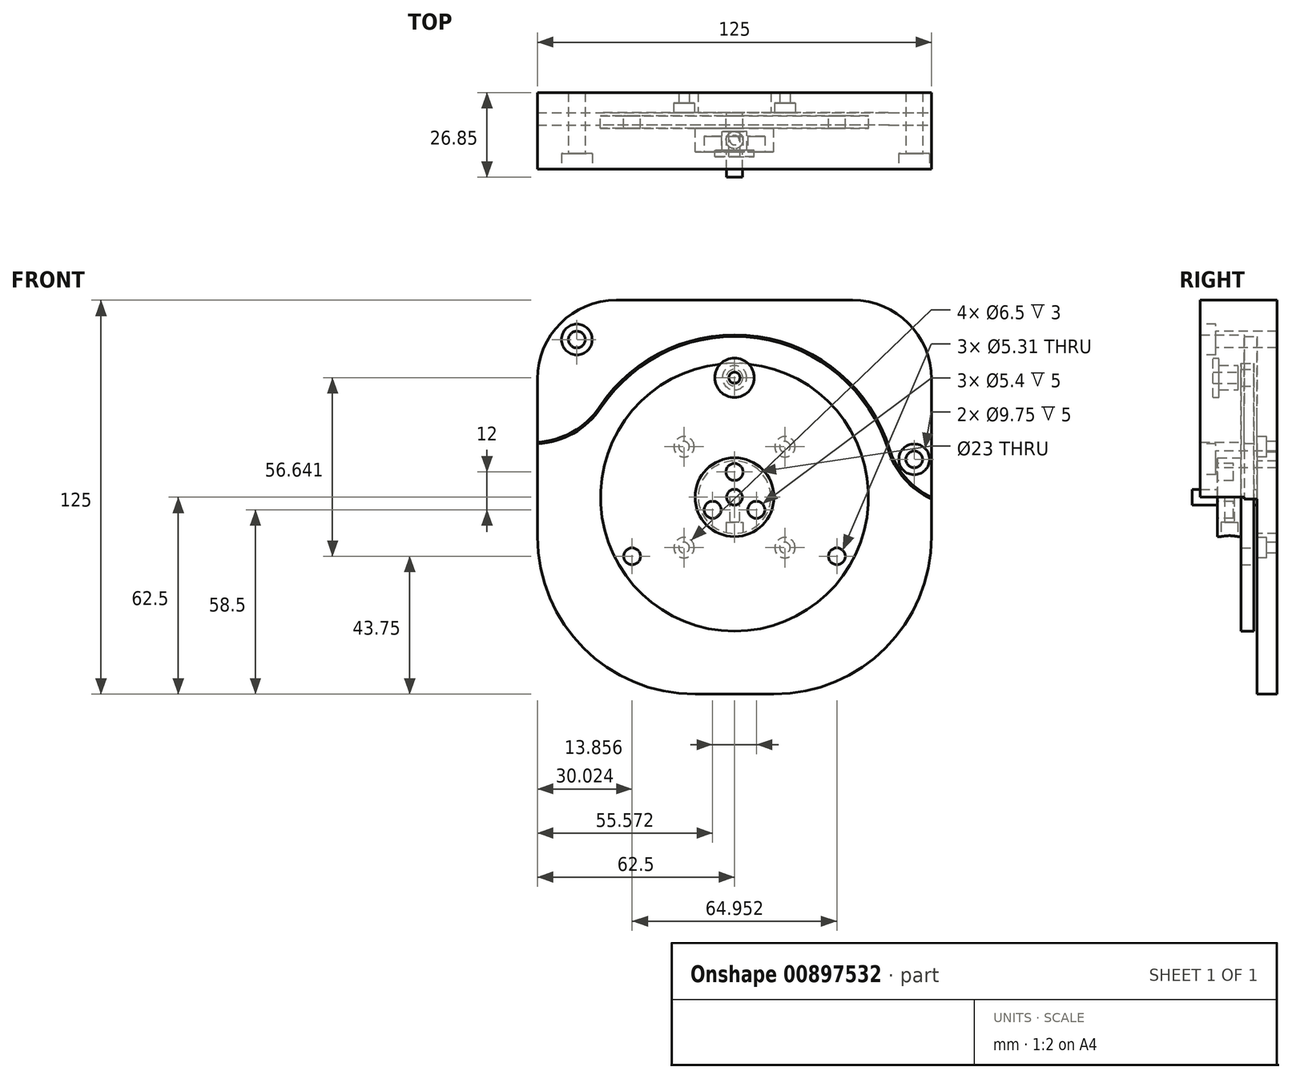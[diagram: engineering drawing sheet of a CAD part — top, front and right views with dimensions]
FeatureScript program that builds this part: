
annotation { "Feature Type Name" : "Feature", "Feature Type Description" : "" }
export const myFeature = defineFeature(function(context is Context, id is Id, definition is map)
    precondition{}
    {
        {
            var Q0;
            Q0=qCreatedBy(makeId("Front.planeOp"),FACE);
            var sketch = newSketch(context, id + "F0", { "sketchPlane" : qUnion([Q0])});
            skLineSegment(sketch, "E0.bottom", {"start": v(62.5, 62.5) * mm, "end": v(-62.5, 62.5) * mm});
            skLineSegment(sketch, "E0.top", {"start": v(62.5, -62.5) * mm, "end": v(-62.5, -62.5) * mm});
            skLineSegment(sketch, "E0.left", {"start": v(62.5, 62.5) * mm, "end": v(62.5, -62.5) * mm});
            skLineSegment(sketch, "E0.right", {"start": v(-62.5, 62.5) * mm, "end": v(-62.5, -62.5) * mm});
            skPoint(sketch, "E0.middle", {"position": v(0, 0) * mm});
            skSolve(sketch);
        }
        {
            var Q0;
            Q0=qCreatedBy(makeId("Front.planeOp"),FACE);
            var sketch = newSketch(context, id + "F1", { "sketchPlane" : qUnion([Q0])});
            skCircle(sketch, "E1", {"center": v(0, 0) * mm, "radius": 11.5 * mm});
            skSolve(sketch);
        }
        {
            var Q0;
            Q0=qCreatedBy(makeId("Front.planeOp"),FACE);
            var sketch = newSketch(context, id + "F2", { "sketchPlane" : qUnion([Q0])});
            skLineSegment(sketch, "E2.bottom", {"start": v(16, 16) * mm, "end": v(-16, 16) * mm, "construction": true});
            skLineSegment(sketch, "E2.top", {"start": v(16, -16) * mm, "end": v(-16, -16) * mm, "construction": true});
            skLineSegment(sketch, "E2.left", {"start": v(16, 16) * mm, "end": v(16, -16) * mm, "construction": true});
            skLineSegment(sketch, "E2.right", {"start": v(-16, 16) * mm, "end": v(-16, -16) * mm, "construction": true});
            skPoint(sketch, "E2.middle", {"position": v(0, 0) * mm});
            skSolve(sketch);
        }
        {
            var Q0;
            Q0 = qSketchRegion(id + "F0", true);
            extrude(context, id + "F3", {"entities" : qUnion([Q0]), "oppositeDirection" : true, "depth" : 6.35 * mm, "offsetDistance" : 25 * mm});
        }
        {
            var Q0;
            Q0=sQuery(id+"F2.wireOp",VERTEX,"E2.bottom.end");
            var Q1;
            Q1=sQuery(id+"F2.wireOp",VERTEX,"E2.bottom.start");
            var Q2;
            Q2=sQuery(id+"F2.wireOp",VERTEX,"E2.top.end");
            var Q3;
            Q3=sQuery(id+"F2.wireOp",VERTEX,"E2.top.start");
            var Q4;
            Q4=makeQuery(id+"F3.opExtrude","SWEPT_BODY",BODY,{"disambiguationData":[OSD([sQuery(id+"F0.wireOp",EDGE,"E0.bottom"),sQuery(id+"F0.wireOp",EDGE,"E0.top"),sQuery(id+"F0.wireOp",EDGE,"E0.left"),sQuery(id+"F0.wireOp",EDGE,"E0.right")])]});
            hole(context, id + "F4", {"style" : HoleStyle.C_BORE, "endStyle" : HoleEndStyle.THROUGH, "standardTappedOrClearance" : lookupTablePath({ "fit" : "Normal", "standard" : "ISO", "size" : "M3", "type" : "Clearance" }), "standardBlindInLast" : lookupTablePath({ "fit" : "Normal", "standard" : "ISO", "engagement" : "75%", "pitch" : "0.5 mm", "size" : "M3", "type" : "Clearance & tapped" }), "holeDiameter" : 3.4 * mm, "cBoreDiameter" : 6.5 * mm, "cBoreDepth" : 3 * mm, "majorDiameter" : 5 * mm, "isTappedThrough" : true, "tappedDepth" : 4.5 * mm, "tapClearance" : 3, "startFromSketch" : true, "locations" : qUnion([Q0, Q1, Q2, Q3]), "scope" : qUnion([Q4])});
        }
        {
            var Q0;
            Q0=makeQuery(id+"F1.imprint","IMPRINT",FACE,{"disambiguationData":[TD([[makeQuery(id+"F1.imprint","IMPRINT",EDGE,{"derivedFrom":sQuery(id+"F1.wireOp",EDGE,"E1")}),1.0]])]});
            extrude(context, id + "F5", {"entities" : qUnion([Q0]), "operationType" : NewBodyOperationType.REMOVE, "endBound" : BoundingType.THROUGH_ALL, "oppositeDirection" : true, "depth" : 25 * mm, "offsetDistance" : 25 * mm});
        }
        {
            var Q0;
            Q0=qCreatedBy(makeId("Front.planeOp"),FACE);
            var sketch = newSketch(context, id + "F6", { "sketchPlane" : qUnion([Q0])});
            skCircle(sketch, "E3", {"center": v(0, 0) * mm, "radius": 2.5 * mm});
            skSolve(sketch);
        }
        {
            var Q0;
            Q0 = qSketchRegion(id + "F6", true);
            extrude(context, id + "F7", {"entities" : qUnion([Q0]), "depth" : (22 - 1.5) * mm, "offsetDistance" : 25 * mm});
        }
        {
            var Q0;
            Q0=qCreatedBy(makeId("Front.planeOp"),FACE);
            var sketch = newSketch(context, id + "F8", { "sketchPlane" : qUnion([Q0])});
            skCircle(sketch, "E4", {"center": v(0, 0) * mm, "radius": 37.5 * mm, "construction": true});
            skCircle(sketch, "E5", {"center": v(0, 37.5) * mm, "radius": 11 * mm, "construction": true});
            skArc(sketch, "E6", {"start": v(51.5, 0) * mm, "mid": v(8.88, 50.73) * mm, "end": v(-48.44, 17.5) * mm});
            skLineSegment(sketch, "E7", {"start": v(0, 51.5) * mm, "end": v(0, 48.5) * mm, "construction": true});
            skCircle(sketch, "E8", {"center": v(0, 0) * mm, "radius": 42.5 * mm});
            skLineSegment(sketch, "E9", {"start": v(-48.44, 17.5) * mm, "end": v(-62.5, 17.5) * mm});
            skLineSegment(sketch, "E10", {"start": v(-62.5, 17.5) * mm, "end": v(-62.5, 62.5) * mm});
            skLineSegment(sketch, "E11", {"start": v(-62.5, 62.5) * mm, "end": v(62.5, 62.5) * mm});
            skLineSegment(sketch, "E12", {"start": v(62.5, 62.5) * mm, "end": v(62.5, 0) * mm});
            skLineSegment(sketch, "E13", {"start": v(62.5, 0) * mm, "end": v(51.5, 0) * mm});
            skCircle(sketch, "E14", {"center": v(0, 37.5) * mm, "radius": 2.65 * mm, "construction": true});
            skLineSegment(sketch, "E15", {"start": v(0, 37.5) * mm, "end": v(0, 0) * mm, "construction": true});
            skLineSegment(sketch, "E16", {"start": v(0, 0) * mm, "end": v(-32.48, -18.75) * mm, "construction": true});
            skLineSegment(sketch, "E17", {"start": v(0, 0) * mm, "end": v(32.48, -18.75) * mm, "construction": true});
            skPoint(sketch, "E18", {"position": v(0, 50) * mm});
            skSolve(sketch);
        }
        {
            var Q0;
            Q0=makeQuery(id+"F8.imprint","IMPRINT",FACE,{"disambiguationData":[TD([[makeQuery(id+"F8.imprint","IMPRINT",EDGE,{"derivedFrom":sQuery(id+"F8.wireOp",EDGE,"E6")}),-1.0]])]});
            extrude(context, id + "F9", {"entities" : qUnion([Q0]), "depth" : 18 * mm, "offsetDistance" : 25 * mm});
        }
        {
            var Q0;
            Q0=qCreatedBy(makeId("Front.planeOp"),FACE);
            cPlane(context, id + "F10", {"entities" : qUnion([Q0]), "cplaneType" : CPlaneType.OFFSET, "offset" : 1 * mm, "width" : 150 * mm, "height" : 150 * mm});
        }
        {
            var Q0;
            Q0=qCreatedBy(id+"F10.planeOp",FACE);
            var sketch = newSketch(context, id + "F11", { "sketchPlane" : qUnion([Q0])});
            skCircle(sketch, "E19.0", {"center": v(0, 0) * mm, "radius": 42.5 * mm});
            skCircle(sketch, "E20", {"center": v(0, 0) * mm, "radius": 2.5 * mm});
            skCircle(sketch, "E21", {"center": v(0, 37.9) * mm, "radius": 2.65 * mm});
            skCircle(sketch, "E22", {"center": v(-32.48, -18.75) * mm, "radius": 2.65 * mm});
            skCircle(sketch, "E23", {"center": v(32.48, -18.75) * mm, "radius": 2.65 * mm});
            skSolve(sketch);
        }
        {
            var Q0;
            Q0 = qSketchRegion(id + "F11", true);
            extrude(context, id + "F12", {"entities" : qUnion([Q0]), "depth" : 4 * mm, "offsetDistance" : 25 * mm});
        }
        {
            var Q0;
            Q0=makeQuery(id+"F12.opExtrude","CAP_FACE",FACE,{"disambiguationData":[OSD([sQuery(id+"F11.wireOp",EDGE,"E19.0"),sQuery(id+"F11.wireOp",EDGE,"E20"),sQuery(id+"F11.wireOp",EDGE,"E21"),sQuery(id+"F11.wireOp",EDGE,"E22"),sQuery(id+"F11.wireOp",EDGE,"E23")])],"isStart":false});
            var sketch = newSketch(context, id + "F13", { "sketchPlane" : qUnion([Q0])});
            skCircle(sketch, "E24", {"center": v(0, 0) * mm, "radius": 12.5 * mm});
            skCircle(sketch, "E25", {"center": v(0, 0) * mm, "radius": 2.5 * mm});
            skSolve(sketch);
        }
        {
            var Q0;
            Q0=makeQuery(id+"F13.imprint","IMPRINT",FACE,{"disambiguationData":[TD([[makeQuery(id+"F13.imprint","IMPRINT",EDGE,{"derivedFrom":sQuery(id+"F13.wireOp",EDGE,"E24")}),1.0]])]});
            extrude(context, id + "F14", {"entities" : qUnion([Q0]), "operationType" : NewBodyOperationType.ADD, "depth" : 7.5 * mm, "offsetDistance" : 25 * mm});
        }
        {
            var Q0;
            Q0=makeQuery(id+"F14.opExtrude","CAP_FACE",FACE,{"disambiguationData":[OSD([sQuery(id+"F13.wireOp",EDGE,"E24"),sQuery(id+"F13.wireOp",EDGE,"E25")])],"isStart":false});
            var sketch = newSketch(context, id + "F15", { "sketchPlane" : qUnion([Q0])});
            skLineSegment(sketch, "E26", {"start": v(0, 0) * mm, "end": v(0, 8) * mm, "construction": true});
            skLineSegment(sketch, "E27", {"start": v(0, 0) * mm, "end": v(6.93, -4) * mm, "construction": true});
            skLineSegment(sketch, "E28", {"start": v(0, 0) * mm, "end": v(-6.93, -4) * mm, "construction": true});
            skCircle(sketch, "E29", {"center": v(0, 8) * mm, "radius": 2.7 * mm});
            skCircle(sketch, "E30", {"center": v(6.93, -4) * mm, "radius": 2.7 * mm});
            skCircle(sketch, "E31", {"center": v(-6.93, -4) * mm, "radius": 2.7 * mm});
            skSolve(sketch);
        }
        {
            var Q0;
            Q0 = qSketchRegion(id + "F15", true);
            extrude(context, id + "F16", {"entities" : qUnion([Q0]), "operationType" : NewBodyOperationType.REMOVE, "oppositeDirection" : true, "depth" : 5 * mm, "offsetDistance" : 25 * mm});
        }
        {
            var Q0;
            Q0=qCreatedBy(makeId("Top.planeOp"),FACE);
            cPlane(context, id + "F17", {"entities" : qUnion([Q0]), "cplaneType" : CPlaneType.OFFSET, "offset" : 13 * mm, "oppositeDirection" : true, "width" : 150 * mm, "height" : 150 * mm});
        }
        {
            var Q0;
            Q0=qCreatedBy(id+"F17.planeOp",FACE);
            var sketch = newSketch(context, id + "F18", { "sketchPlane" : qUnion([Q0])});
            skCircle(sketch, "E32", {"center": v(0, -8.75) * mm, "radius": 2.7 * mm, "construction": true});
            skLineSegment(sketch, "E33.0", {"start": v(12.5, -12.5) * mm, "end": v(-12.5, -12.5) * mm, "construction": true});
            skLineSegment(sketch, "E34.0", {"start": v(12.5, -5) * mm, "end": v(-12.5, -5) * mm, "construction": true});
            skLineSegment(sketch, "E35", {"start": v(0, -12.5) * mm, "end": v(0, -5) * mm, "construction": true});
            skCircle(sketch, "E36", {"center": v(0, -8.75) * mm, "radius": 1.5 * mm});
            skSolve(sketch);
        }
        {
            var Q0;
            Q0=makeQuery(id+"F18.imprint","IMPRINT",FACE,{"disambiguationData":[TD([[makeQuery(id+"F18.imprint","IMPRINT",EDGE,{"derivedFrom":sQuery(id+"F18.wireOp",EDGE,"E36")}),1.0]])]});
            extrude(context, id + "F19", {"entities" : qUnion([Q0]), "operationType" : NewBodyOperationType.REMOVE, "depth" : 13 * mm, "offsetDistance" : 25 * mm});
        }
        {
            var Q0;
            Q0=qCreatedBy(id+"F17.planeOp",FACE);
            var sketch = newSketch(context, id + "F20", { "sketchPlane" : qUnion([Q0])});
            skCircle(sketch, "E37.0", {"center": v(0, -8.75) * mm, "radius": 1.5 * mm});
            skCircle(sketch, "E38", {"center": v(0, -8.75) * mm, "radius": 2.7 * mm});
            skSolve(sketch);
        }
        {
            var Q0;
            Q0=makeQuery(id+"F20.imprint","IMPRINT",FACE,{"disambiguationData":[TD([[makeQuery(id+"F20.imprint","IMPRINT",EDGE,{"derivedFrom":sQuery(id+"F20.wireOp",EDGE,"E37.0")}),-1.0]])]});
            var Q1;
            Q1=makeQuery(id+"F20.imprint","IMPRINT",FACE,{"disambiguationData":[TD([[makeQuery(id+"F20.imprint","IMPRINT",EDGE,{"derivedFrom":sQuery(id+"F20.wireOp",EDGE,"E37.0")}),1.0]])]});
            extrude(context, id + "F21", {"entities" : qUnion([Q0, Q1]), "operationType" : NewBodyOperationType.REMOVE, "depth" : 5 * mm, "offsetDistance" : 25 * mm});
        }
        {
            var Q0;
            Q0=makeQuery(id+"F9.opExtrude","CAP_FACE",FACE,{"disambiguationData":[OSD([sQuery(id+"F8.wireOp",EDGE,"E6"),sQuery(id+"F8.wireOp",EDGE,"E9"),sQuery(id+"F8.wireOp",EDGE,"E10"),sQuery(id+"F8.wireOp",EDGE,"E11"),sQuery(id+"F8.wireOp",EDGE,"E12"),sQuery(id+"F8.wireOp",EDGE,"E13")])],"isStart":false});
            var sketch = newSketch(context, id + "F22", { "sketchPlane" : qUnion([Q0])});
            skPoint(sketch, "E39", {"position": v(57, 12) * mm});
            skPoint(sketch, "E40", {"position": v(-50, 50) * mm});
            skSolve(sketch);
        }
        {
            var Q0;
            Q0=sQuery(id+"F22.wireOp",VERTEX,"E39");
            var Q1;
            Q1=sQuery(id+"F22.wireOp",VERTEX,"E40");
            var Q2;
            Q2=makeQuery(id+"F9.opExtrude","SWEPT_BODY",BODY,{"disambiguationData":[OSD([sQuery(id+"F8.wireOp",EDGE,"E6"),sQuery(id+"F8.wireOp",EDGE,"E9"),sQuery(id+"F8.wireOp",EDGE,"E10"),sQuery(id+"F8.wireOp",EDGE,"E11"),sQuery(id+"F8.wireOp",EDGE,"E12"),sQuery(id+"F8.wireOp",EDGE,"E13")])]});
            var Q3;
            Q3=makeQuery(id+"F3.opExtrude","SWEPT_BODY",BODY,{"disambiguationData":[OSD([sQuery(id+"F0.wireOp",EDGE,"E0.bottom"),sQuery(id+"F0.wireOp",EDGE,"E0.top"),sQuery(id+"F0.wireOp",EDGE,"E0.left"),sQuery(id+"F0.wireOp",EDGE,"E0.right")])]});
            hole(context, id + "F23", {"style" : HoleStyle.C_BORE, "endStyle" : HoleEndStyle.THROUGH, "standardTappedOrClearance" : lookupTablePath({ "fit" : "Close", "standard" : "ISO", "size" : "M5", "type" : "Clearance" }), "standardBlindInLast" : lookupTablePath({ "fit" : "Close", "standard" : "ISO", "engagement" : "75%", "pitch" : "0.8 mm", "size" : "M5", "type" : "Clearance & tapped" }), "holeDiameter" : 5.3 * mm, "cBoreDiameter" : 9.75 * mm, "cBoreDepth" : 5 * mm, "majorDiameter" : 5 * mm, "isTappedThrough" : true, "tappedDepth" : 4.5 * mm, "tapClearance" : 3, "startFromSketch" : true, "locations" : qUnion([Q0, Q1]), "scope" : qUnion([Q2, Q3])});
        }
        {
            var Q0;
            Q0=makeQuery(id+"F12.opExtrude","CAP_FACE",FACE,{"disambiguationData":[OSD([sQuery(id+"F11.wireOp",EDGE,"E19.0"),sQuery(id+"F11.wireOp",EDGE,"E20"),sQuery(id+"F11.wireOp",EDGE,"E21"),sQuery(id+"F11.wireOp",EDGE,"E22"),sQuery(id+"F11.wireOp",EDGE,"E23")])],"isStart":false});
            cPlane(context, id + "F24", {"entities" : qUnion([Q0]), "cplaneType" : CPlaneType.OFFSET, "offset" : 3.5 * mm, "width" : 150 * mm, "height" : 150 * mm});
        }
        {
            var Q0;
            Q0=qCreatedBy(id+"F24.planeOp",FACE);
            var sketch = newSketch(context, id + "F25", { "sketchPlane" : qUnion([Q0])});
            skPoint(sketch, "E41.0", {"position": v(0, 50) * mm});
            skCircle(sketch, "E42", {"center": v(0, 0) * mm, "radius": 50 * mm});
            skSolve(sketch);
        }
        {
            var Q0;
            Q0=qCreatedBy(makeId("Right.planeOp"),FACE);
            var sketch = newSketch(context, id + "F26", { "sketchPlane" : qUnion([Q0])});
            skCircle(sketch, "E43", {"center": v(-8.5, 50) * mm, "radius": 4 * mm});
            skSolve(sketch);
        }
        {
            var Q0;
            Q0=makeQuery(id+"F9.opExtrude","SWEPT_EDGE",EDGE,{"disambiguationData":[OSD([sQuery(id+"F8.wireOp",EDGE,"E6"),sQuery(id+"F8.wireOp",EDGE,"E9")])]});
            var Q1;
            Q1=makeQuery(id+"F9.opExtrude","SWEPT_EDGE",EDGE,{"disambiguationData":[OSD([sQuery(id+"F8.wireOp",EDGE,"E6"),sQuery(id+"F8.wireOp",EDGE,"E13")])]});
            var Q2;
            Q2=makeQuery(id+"F9.opExtrude","SWEPT_EDGE",EDGE,{"disambiguationData":[OSD([sQuery(id+"F8.wireOp",EDGE,"E10"),sQuery(id+"F8.wireOp",EDGE,"E11")])]});
            var Q3;
            Q3=makeQuery(id+"F3.opExtrude","SWEPT_EDGE",EDGE,{"disambiguationData":[OSD([sQuery(id+"F0.wireOp",EDGE,"E0.bottom"),sQuery(id+"F0.wireOp",EDGE,"E0.right")])]});
            var Q4;
            Q4=makeQuery(id+"F9.opExtrude","SWEPT_EDGE",EDGE,{"disambiguationData":[OSD([sQuery(id+"F8.wireOp",EDGE,"E11"),sQuery(id+"F8.wireOp",EDGE,"E12")])]});
            var Q5;
            Q5=makeQuery(id+"F3.opExtrude","SWEPT_EDGE",EDGE,{"disambiguationData":[OSD([sQuery(id+"F0.wireOp",EDGE,"E0.bottom"),sQuery(id+"F0.wireOp",EDGE,"E0.left")])]});
            fillet(context, id + "F27", {"entities" : qUnion([Q0, Q1, Q2, Q3, Q4, Q5]), "tangentPropagation" : true, "radius" : 25 * mm, "defaultsChanged" : false, "vertexSettings" : [], "allowEdgeOverflow" : false});
        }
        {
            var Q0;
            Q0=makeQuery(id+"F3.opExtrude","CAP_FACE",FACE,{"disambiguationData":[OSD([sQuery(id+"F0.wireOp",EDGE,"E0.bottom"),sQuery(id+"F0.wireOp",EDGE,"E0.top"),sQuery(id+"F0.wireOp",EDGE,"E0.left"),sQuery(id+"F0.wireOp",EDGE,"E0.right")])],"isStart":true});
            var sketch = newSketch(context, id + "F28", { "sketchPlane" : qUnion([Q0])});
            skSolve(sketch);
        }
        {
            var Q0;
            {var subQ2=sQuery(id+"F0.wireOp",EDGE,"E0.top");Q0=makeQuery(id+"F28.imprint","IMPRINT",FACE,{"disambiguationData":[TD([[makeQuery(id+"F28.imprint","IMPRINT",EDGE,{"derivedFrom":makeQuery(id+"F3.opExtrude","CAP_EDGE",EDGE,{"disambiguationData":[OSD([subQ2])],"isStart":true})}),-1.0]])]});}
            var sketch = newSketch(context, id + "F29", { "sketchPlane" : qUnion([Q0])});
            skArc(sketch, "E44.0", {"start": v(-42.83, 28.6) * mm, "mid": v(-51.34, 20.7) * mm, "end": v(-62.5, 17.5) * mm, "construction": true});
            skArc(sketch, "E45.0", {"start": v(49.19, 15.25) * mm, "mid": v(7.39, 50.97) * mm, "end": v(-42.83, 28.6) * mm, "construction": true});
            skArc(sketch, "E46.0", {"start": v(62.5, 0) * mm, "mid": v(54.23, 6.22) * mm, "end": v(49.19, 15.25) * mm, "construction": true});
            skCircle(sketch, "E47.0", {"center": v(0, 0) * mm, "radius": 42.5 * mm, "construction": true});
            skArc(sketch, "E48.0", {"start": v(-42.42, 28.32) * mm, "mid": v(-51.1, 20.26) * mm, "end": v(-62.5, 17) * mm});
            skArc(sketch, "E48.1", {"start": v(48.71, 15.1) * mm, "mid": v(7.32, 50.47) * mm, "end": v(-42.42, 28.32) * mm});
            skArc(sketch, "E48.2", {"start": v(62.5, -0.55) * mm, "mid": v(53.93, 5.8) * mm, "end": v(48.71, 15.1) * mm});
            skCircle(sketch, "E49.0", {"center": v(0, 0) * mm, "radius": 43.5 * mm});
            skLineSegment(sketch, "E50", {"start": v(-62.5, 17) * mm, "end": v(-62.5, -8) * mm});
            skLineSegment(sketch, "E51", {"start": v(-62.5, -8) * mm, "end": v(-42.76, -8) * mm});
            skLineSegment(sketch, "E52", {"start": v(62.5, -0.55) * mm, "end": v(62.5, -8) * mm});
            skLineSegment(sketch, "E53", {"start": v(62.5, -8) * mm, "end": v(42.76, -8) * mm});
            skSolve(sketch);
        }
        {
            var Q0;
            Q0=makeQuery(id+"F29.imprint","IMPRINT",FACE,{"disambiguationData":[TD([[makeQuery(id+"F29.imprint","IMPRINT",EDGE,{"derivedFrom":sQuery(id+"F29.wireOp",EDGE,"E48.0")}),1.0]])]});
            extrude(context, id + "F30", {"entities" : qUnion([Q0]), "operationType" : NewBodyOperationType.ADD, "depth" : 4 * mm, "offsetDistance" : 25 * mm});
        }
        {
            var Q0;
            Q0=makeQuery(id+"F3.opExtrude","SWEPT_EDGE",EDGE,{"disambiguationData":[OSD([sQuery(id+"F0.wireOp",EDGE,"E0.top"),sQuery(id+"F0.wireOp",EDGE,"E0.right")])]});
            var Q1;
            Q1=makeQuery(id+"F3.opExtrude","SWEPT_EDGE",EDGE,{"disambiguationData":[OSD([sQuery(id+"F0.wireOp",EDGE,"E0.top"),sQuery(id+"F0.wireOp",EDGE,"E0.left")])]});
            fillet(context, id + "F31", {"entities" : qUnion([Q0, Q1]), "tangentPropagation" : true, "radius" : 50 * mm, "defaultsChanged" : true, "vertexSettings" : [], "allowEdgeOverflow" : false});
        }
        {
            var Q0;
            Q0=makeQuery(id+"F12.opExtrude","CAP_FACE",FACE,{"disambiguationData":[OSD([sQuery(id+"F11.wireOp",EDGE,"E19.0"),sQuery(id+"F11.wireOp",EDGE,"E20"),sQuery(id+"F11.wireOp",EDGE,"E21"),sQuery(id+"F11.wireOp",EDGE,"E22"),sQuery(id+"F11.wireOp",EDGE,"E23")])],"isStart":false});
            cPlane(context, id + "F32", {"entities" : qUnion([Q0]), "cplaneType" : CPlaneType.OFFSET, "offset" : 1 * mm, "width" : 150 * mm, "height" : 150 * mm});
        }
        {
            var Q0;
            Q0=qCreatedBy(id+"F32.planeOp",FACE);
            var sketch = newSketch(context, id + "F33", { "sketchPlane" : qUnion([Q0])});
            skCircle(sketch, "E54.0", {"center": v(0, 37.9) * mm, "radius": 2.65 * mm, "construction": true});
            skCircle(sketch, "E55", {"center": v(0, 37.9) * mm, "radius": 3.88 * mm});
            skCircle(sketch, "E56", {"center": v(0, 37.9) * mm, "radius": 1.75 * mm});
            skSolve(sketch);
        }
        {
            var Q0;
            Q0 = qSketchRegion(id + "F33", true);
            extrude(context, id + "F34", {"entities" : qUnion([Q0]), "depth" : 6 * mm, "offsetDistance" : 25 * mm});
        }
        {
            var Q0;
            Q0=makeQuery(id+"F34.opExtrude","CAP_FACE",FACE,{"disambiguationData":[OSD([sQuery(id+"F33.wireOp",EDGE,"E55"),sQuery(id+"F33.wireOp",EDGE,"E56")])],"isStart":false});
            var sketch = newSketch(context, id + "F35", { "sketchPlane" : qUnion([Q0])});
            skCircle(sketch, "E57.0", {"center": v(0, 37.9) * mm, "radius": 1.75 * mm});
            skCircle(sketch, "E58", {"center": v(0, 37.9) * mm, "radius": 6.25 * mm});
            skSolve(sketch);
        }
        {
            var Q0;
            Q0 = qSketchRegion(id + "F35", true);
            extrude(context, id + "F36", {"entities" : qUnion([Q0]), "operationType" : NewBodyOperationType.ADD, "depth" : 2 * mm, "offsetDistance" : 25 * mm});
        }
    });
